# Revit family: 0056235 Lighting Fixture_Sylvania_Sylproof Superia Polyc-T5 Electronic Ballast_Ceiling Pendant
name_source: partatom
category: Lighting Fixtures
revit_build: Autodesk Revit 2017 (Build: 20190507_1515(x64)
units: mm (PartAtom-declared; Revit-internal decimal feet)

## family parameters
Cut with Voids When Loaded = No
Host = Face
Light Source = Yes
OmniClass Number = 23.80.70.11.17
OmniClass Title = Specialized Lighting by Location or Use
Part Type = Normal
Room Calculation Point = No
Round Connector Dimension = Use Diameter
Shared = No

## types (1)
- Sylproof Superia PC T5 16mmØ 2x49W lamp with A2 ballast
    Apparent Load = 98 VA
    Assembly Code = D5020200
    Body Material = Polycarbonate_Body_Sylvania_Brite White
    Bracket-Diffuser Material = Stainless Steel_Bracket_Sylvania_Grey
    Bracket-Mounting Material = Stainless Steel_Bracket_Sylvania_Grey
    Catalog Number = 0056235 Sylproof Superia PC T5 16mmØ 2x49W lamp with A2 ballast
    Celma/IEE = A2
    Color Filter = 16777215
    Default Elevation = 0 mm  [stored 0 ft]
    Description = Polycarbonate body & diffuser. Stainless steel fixing
    Diffuser Brackets Length = 1405 mm  [stored 4.60958 ft]
    Diffuser Material = Polycarbonate_Diffuser_Sylvania_Clear
    Dimming Lamp Color Temperature Shift = <None>
    Electrical Protection = Class I
    Emit Shape Visible in Rendering = No
    Emit from Rectangle Length = 1545 mm
    Emit from Rectangle Width = 64 mm
    Glow Wire Test = 850 °C
    Height = 99 mm
    IK Rating = 07
    IP Rating = 65
    LOR = 68%
    Lamp = 2 x 49W
    Lamp - Single = No
    Lamp - Twin = Yes
    Lamp Comments = 2 x 49W T16 G5
    Lamp Material = Acrylic High Luminance Glass_Lamp_Sylvania_White
    Length = 1565 mm
    Length Help = 1505 mm
    Manufacturer = Feilo Sylvania
    Model = Sylproof Superia PC T5 16mmØ 2x49W lamp with A2 ballast
    Mounting Brackets Length = 930 mm
    Mounting Brackets Width = 41 mm  [stored 0.134514 ft]
    Mounting Height = 1000 mm  [stored 3.28084 ft]
    Number of Diffuser Brackets = 3
    Photometric Web File = 0056235_sylproofSuperiaPolycorbonatediffucerT52x49WElectronic-77636.ies
    Product Family = SYLPROOF SUPERIA POLYCARBONATE - T5 ELECTRONIC BALLAST
    Product Page URL = http://www.sylvania-lighting.com
    Side Void Width = 43 mm
    T Class Max = 25 °C
    T Class Min = 0 °C
    Tilt Angle = -90.00°
    URL = http://www.sylvania-lighting.com
    Voltage = 230 V
    Voltage Comments = UNV (Universal Voltage; 220-240 Volt)
    Weight = 2.25 kg
    Width = 92 mm
    Width Help = 24 mm  [stored 0.0787402 ft]

note: [stored X ft] marks values corroborated as IEEE doubles in the binary element streams (Revit-internal decimal feet)

## geometry (parser evidence)
native form markers: Sweep x11
no freeform markers — native parametric forms only
